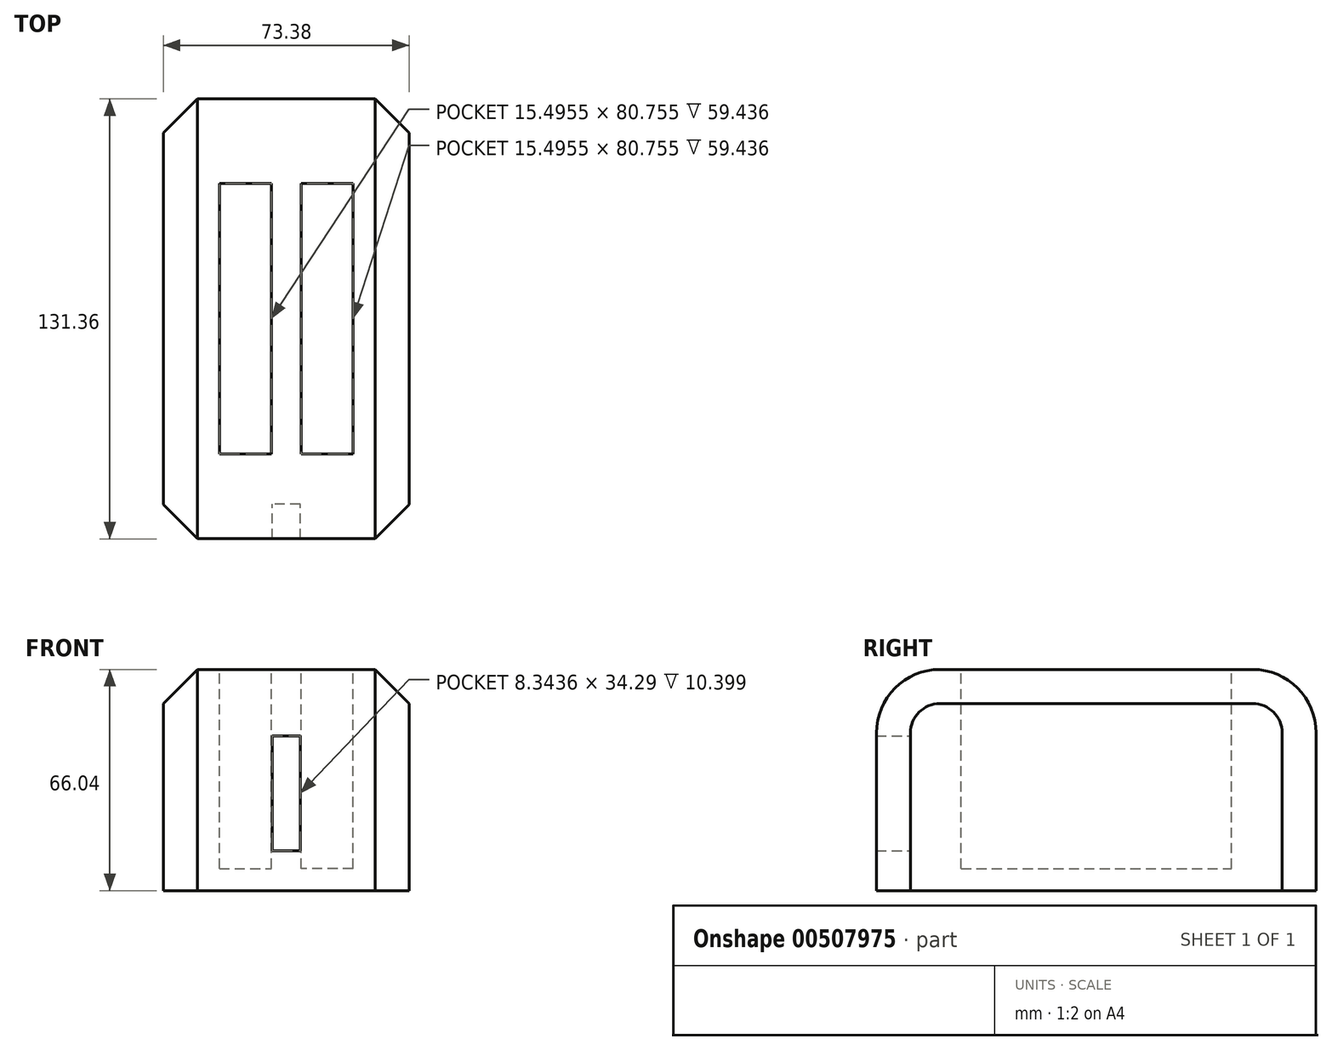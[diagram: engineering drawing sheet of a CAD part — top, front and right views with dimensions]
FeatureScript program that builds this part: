
annotation { "Feature Type Name" : "Feature", "Feature Type Description" : "" }
export const myFeature = defineFeature(function(context is Context, id is Id, definition is map)
    precondition{}
    {
        {
            var Q0;
            Q0=qCreatedBy(makeId("Top.planeOp"),FACE);
            var sketch = newSketch(context, id + "F0", { "sketchPlane" : qUnion([Q0])});
            skLineSegment(sketch, "E0.bottom", {"start": v(36.69, 65.68) * mm, "end": v(-36.69, 65.68) * mm});
            skLineSegment(sketch, "E0.top", {"start": v(36.69, -65.68) * mm, "end": v(-36.69, -65.68) * mm});
            skLineSegment(sketch, "E0.left", {"start": v(36.69, 65.68) * mm, "end": v(36.69, -65.68) * mm});
            skLineSegment(sketch, "E0.right", {"start": v(-36.69, 65.68) * mm, "end": v(-36.69, -65.68) * mm});
            skPoint(sketch, "E0.middle", {"position": v(0, 0) * mm});
            skSolve(sketch);
        }
        {
            var Q0;
            Q0=makeQuery(id+"F0.imprint","IMPRINT",FACE,{"disambiguationData":[TD([[makeQuery(id+"F0.imprint","IMPRINT",EDGE,{"derivedFrom":sQuery(id+"F0.wireOp",EDGE,"E0.bottom")}),1.0]])]});
            extrude(context, id + "F1", {"entities" : qUnion([Q0]), "depth" : 66.04 * mm});
        }
        {
            var Q0;
            Q0=makeQuery(id+"F1.opExtrude","CAP_EDGE",EDGE,{"disambiguationData":[OSD([sQuery(id+"F0.wireOp",EDGE,"E0.bottom")])],"isStart":false});
            var Q1;
            Q1=makeQuery(id+"F1.opExtrude","CAP_EDGE",EDGE,{"disambiguationData":[OSD([sQuery(id+"F0.wireOp",EDGE,"E0.top")])],"isStart":false});
            fillet(context, id + "F2", {"entities" : qUnion([Q0, Q1]), "radius" : 19 * mm, "tangentPropagation" : true, "allowEdgeOverflow" : false});
        }
        {
            var Q0;
            Q0=makeQuery(id+"F1.opExtrude","CAP_EDGE",EDGE,{"disambiguationData":[OSD([sQuery(id+"F0.wireOp",EDGE,"E0.right")])],"isStart":false});
            var Q1;
            Q1=makeQuery(id+"F2.opFillet","BLEND_EDGE",EDGE,{"blendedFrom":[makeQuery(id+"F1.opExtrude","CAP_EDGE",EDGE,{"disambiguationData":[OSD([sQuery(id+"F0.wireOp",EDGE,"E0.bottom")])],"isStart":false}),makeQuery(id+"F1.opExtrude","SWEPT_FACE",FACE,{"disambiguationData":[OSD([sQuery(id+"F0.wireOp",EDGE,"E0.right")])]})],"blendedInto":[makeQuery(id+"F1.opExtrude","SWEPT_FACE",FACE,{"disambiguationData":[OSD([sQuery(id+"F0.wireOp",EDGE,"E0.right")])]})]});
            var Q2;
            Q2=makeQuery(id+"F1.opExtrude","SWEPT_EDGE",EDGE,{"disambiguationData":[OSD([sQuery(id+"F0.wireOp",EDGE,"E0.bottom"),sQuery(id+"F0.wireOp",EDGE,"E0.right")])]});
            var Q3;
            Q3=makeQuery(id+"F2.opFillet","BLEND_EDGE",EDGE,{"blendedFrom":[makeQuery(id+"F1.opExtrude","CAP_EDGE",EDGE,{"disambiguationData":[OSD([sQuery(id+"F0.wireOp",EDGE,"E0.top")])],"isStart":false}),makeQuery(id+"F1.opExtrude","SWEPT_FACE",FACE,{"disambiguationData":[OSD([sQuery(id+"F0.wireOp",EDGE,"E0.right")])]})],"blendedInto":[makeQuery(id+"F1.opExtrude","SWEPT_FACE",FACE,{"disambiguationData":[OSD([sQuery(id+"F0.wireOp",EDGE,"E0.right")])]})]});
            var Q4;
            Q4=makeQuery(id+"F1.opExtrude","SWEPT_EDGE",EDGE,{"disambiguationData":[OSD([sQuery(id+"F0.wireOp",EDGE,"E0.top"),sQuery(id+"F0.wireOp",EDGE,"E0.right")])]});
            var Q5;
            Q5=makeQuery(id+"F1.opExtrude","CAP_EDGE",EDGE,{"disambiguationData":[OSD([sQuery(id+"F0.wireOp",EDGE,"E0.left")])],"isStart":false});
            var Q6;
            Q6=makeQuery(id+"F2.opFillet","BLEND_EDGE",EDGE,{"blendedFrom":[makeQuery(id+"F1.opExtrude","CAP_EDGE",EDGE,{"disambiguationData":[OSD([sQuery(id+"F0.wireOp",EDGE,"E0.bottom")])],"isStart":false}),makeQuery(id+"F1.opExtrude","SWEPT_FACE",FACE,{"disambiguationData":[OSD([sQuery(id+"F0.wireOp",EDGE,"E0.left")])]})],"blendedInto":[makeQuery(id+"F1.opExtrude","SWEPT_FACE",FACE,{"disambiguationData":[OSD([sQuery(id+"F0.wireOp",EDGE,"E0.left")])]})]});
            var Q7;
            Q7=makeQuery(id+"F1.opExtrude","SWEPT_EDGE",EDGE,{"disambiguationData":[OSD([sQuery(id+"F0.wireOp",EDGE,"E0.bottom"),sQuery(id+"F0.wireOp",EDGE,"E0.left")])]});
            var Q8;
            Q8=makeQuery(id+"F2.opFillet","BLEND_EDGE",EDGE,{"blendedFrom":[makeQuery(id+"F1.opExtrude","CAP_EDGE",EDGE,{"disambiguationData":[OSD([sQuery(id+"F0.wireOp",EDGE,"E0.top")])],"isStart":false}),makeQuery(id+"F1.opExtrude","SWEPT_FACE",FACE,{"disambiguationData":[OSD([sQuery(id+"F0.wireOp",EDGE,"E0.left")])]})],"blendedInto":[makeQuery(id+"F1.opExtrude","SWEPT_FACE",FACE,{"disambiguationData":[OSD([sQuery(id+"F0.wireOp",EDGE,"E0.left")])]})]});
            var Q9;
            Q9=makeQuery(id+"F1.opExtrude","SWEPT_EDGE",EDGE,{"disambiguationData":[OSD([sQuery(id+"F0.wireOp",EDGE,"E0.top"),sQuery(id+"F0.wireOp",EDGE,"E0.left")])]});
            chamfer(context, id + "F3", {"entities" : qUnion([Q0, Q1, Q2, Q3, Q4, Q5, Q6, Q7, Q8, Q9]), "width" : 10.16 * mm, "tangentPropagation" : true});
        }
        {
            var Q0;
            Q0=makeQuery(id+"F1.opExtrude","CAP_FACE",FACE,{"disambiguationData":[OSD([sQuery(id+"F0.wireOp",EDGE,"E0.bottom"),sQuery(id+"F0.wireOp",EDGE,"E0.top"),sQuery(id+"F0.wireOp",EDGE,"E0.left"),sQuery(id+"F0.wireOp",EDGE,"E0.right")])],"isStart":false});
            var sketch = newSketch(context, id + "F4", { "sketchPlane" : qUnion([Q0])});
            skLineSegment(sketch, "E1.bottom", {"start": v(19.97, -40.38) * mm, "end": v(4.47, -40.38) * mm});
            skLineSegment(sketch, "E1.top", {"start": v(19.97, 40.38) * mm, "end": v(4.47, 40.38) * mm});
            skLineSegment(sketch, "E1.left", {"start": v(19.97, -40.38) * mm, "end": v(19.97, 40.38) * mm});
            skLineSegment(sketch, "E1.right", {"start": v(4.47, -40.38) * mm, "end": v(4.47, 40.38) * mm});
            skPoint(sketch, "E1.middle", {"position": v(12.22, 0) * mm});
            skLineSegment(sketch, "E2.MirrorCS", {"start": v(-4.47, -40.38) * mm, "end": v(-4.47, 40.38) * mm});
            skLineSegment(sketch, "E3.MirrorCS", {"start": v(-19.97, 40.38) * mm, "end": v(-4.47, 40.38) * mm});
            skLineSegment(sketch, "E4.MirrorCS", {"start": v(-19.97, -40.38) * mm, "end": v(-19.97, 40.38) * mm});
            skLineSegment(sketch, "E5.MirrorCS", {"start": v(-19.97, -40.38) * mm, "end": v(-4.47, -40.38) * mm});
            skSolve(sketch);
        }
        {
            var Q0;
            Q0=makeQuery(id+"F4.imprint","IMPRINT",FACE,{"disambiguationData":[TD([[makeQuery(id+"F4.imprint","IMPRINT",EDGE,{"derivedFrom":sQuery(id+"F4.wireOp",EDGE,"E1.bottom")}),-1.0]])]});
            var Q1;
            Q1=makeQuery(id+"F4.imprint","IMPRINT",FACE,{"disambiguationData":[TD([[makeQuery(id+"F4.imprint","IMPRINT",EDGE,{"derivedFrom":sQuery(id+"F4.wireOp",EDGE,"E2.MirrorCS")}),1.0]])]});
            extrude(context, id + "F5", {"entities" : qUnion([Q0, Q1]), "operationType" : NewBodyOperationType.REMOVE, "oppositeDirection" : true, "depth" : 59.44 * mm});
        }
        {
            var Q0;
            Q0=makeQuery(id+"F1.opExtrude","CAP_FACE",FACE,{"disambiguationData":[OSD([sQuery(id+"F0.wireOp",EDGE,"E0.bottom"),sQuery(id+"F0.wireOp",EDGE,"E0.top"),sQuery(id+"F0.wireOp",EDGE,"E0.left"),sQuery(id+"F0.wireOp",EDGE,"E0.right")])],"isStart":false});
            var sketch = newSketch(context, id + "F6", { "sketchPlane" : qUnion([Q0])});
            skLineSegment(sketch, "E6.bottom", {"start": v(4.17, -92.82) * mm, "end": v(-4.17, -92.82) * mm});
            skLineSegment(sketch, "E6.top", {"start": v(4.17, -55.28) * mm, "end": v(-4.17, -55.28) * mm});
            skLineSegment(sketch, "E6.left", {"start": v(4.17, -92.82) * mm, "end": v(4.17, -55.28) * mm});
            skLineSegment(sketch, "E6.right", {"start": v(-4.17, -92.82) * mm, "end": v(-4.17, -55.28) * mm});
            skPoint(sketch, "E6.middle", {"position": v(0, -74.05) * mm});
            skSolve(sketch);
        }
        {
            var Q0;
            Q0=makeQuery(id+"F6.imprint","IMPRINT",FACE,{"disambiguationData":[TD([[makeQuery(id+"F6.imprint","IMPRINT",EDGE,{"derivedFrom":sQuery(id+"F6.wireOp",EDGE,"E6.bottom")}),-1.0]])]});
            extrude(context, id + "F7", {"entities" : qUnion([Q0]), "operationType" : NewBodyOperationType.REMOVE, "oppositeDirection" : true, "depth" : 54.1 * mm, "hasSecondDirection" : true, "secondDirectionOppositeDirection" : true, "secondDirectionDepth" : 19.8 * mm});
        }
    });
